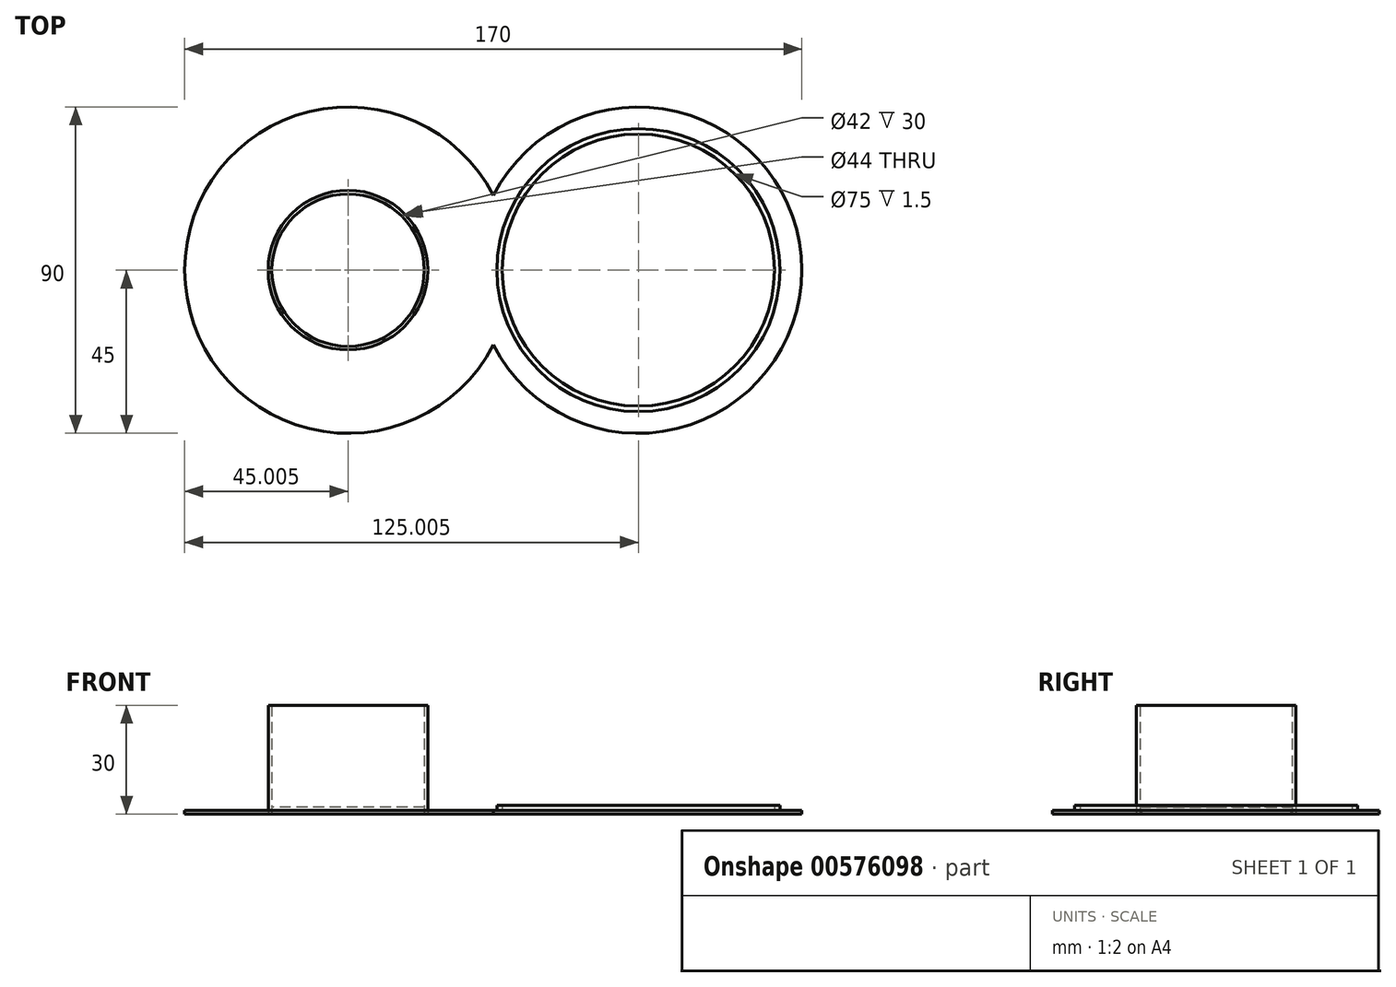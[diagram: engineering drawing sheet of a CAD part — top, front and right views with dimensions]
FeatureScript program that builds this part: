
annotation { "Feature Type Name" : "Feature", "Feature Type Description" : "" }
export const myFeature = defineFeature(function(context is Context, id is Id, definition is map)
    precondition{}
    {
        {
            var Q0;
            Q0=qCreatedBy(makeId("Top.planeOp"),FACE);
            var sketch = newSketch(context, id + "F0", { "sketchPlane" : qUnion([Q0])});
            skCircle(sketch, "E0", {"center": v(-68.95, 0) * mm, "radius": 45 * mm});
            skCircle(sketch, "E1", {"center": v(11.05, 0) * mm, "radius": 45 * mm});
            skCircle(sketch, "E2", {"center": v(-68.95, 0) * mm, "radius": 22 * mm});
            skCircle(sketch, "E3", {"center": v(11.05, 0) * mm, "radius": 39 * mm});
            skCircle(sketch, "E4", {"center": v(-68.95, 0) * mm, "radius": 21 * mm});
            skCircle(sketch, "E5", {"center": v(11.05, 0) * mm, "radius": 37.5 * mm});
            skSolve(sketch);
        }
        {
            var Q0;
            {var subQ3=sQuery(id+"F0.wireOp",EDGE,"E0");var subQ5=sQuery(id+"F0.wireOp",EDGE,"E3");var subQ6=makeQuery(id+"F0.imprint","INTERSECT",VERTEX,{"disambiguationData":[OD(0.0)],"derivedFrom":[subQ3,subQ5]});Q0=makeQuery(id+"F0.imprint","IMPRINT",FACE,{"disambiguationData":[TD([[makeQuery(id+"F0.imprint","IMPRINT",EDGE,{"disambiguationData":[TD([[subQ6,-1.0]])],"derivedFrom":subQ3}),-1.0]])]});}
            var Q1;
            {var subQ0=sQuery(id+"F0.wireOp",EDGE,"E5");var subQ1=sQuery(id+"F0.wireOp",EDGE,"E0");var subQ2=makeQuery(id+"F0.imprint","INTERSECT",VERTEX,{"disambiguationData":[OD(0.0)],"derivedFrom":[subQ1,subQ0]});Q1=makeQuery(id+"F0.imprint","IMPRINT",FACE,{"disambiguationData":[TD([[makeQuery(id+"F0.imprint","IMPRINT",EDGE,{"disambiguationData":[TD([[subQ2,1.0]])],"derivedFrom":subQ1}),-1.0]])]});}
            var Q2;
            Q2=makeQuery(id+"F0.imprint","IMPRINT",FACE,{"disambiguationData":[TD([[makeQuery(id+"F0.imprint","IMPRINT",EDGE,{"derivedFrom":sQuery(id+"F0.wireOp",EDGE,"E2")}),-1.0]])]});
            var Q3;
            {var subQ0=sQuery(id+"F0.wireOp",EDGE,"E3");var subQ1=sQuery(id+"F0.wireOp",EDGE,"E0");var subQ2=makeQuery(id+"F0.imprint","INTERSECT",VERTEX,{"disambiguationData":[OD(0.0)],"derivedFrom":[subQ1,subQ0]});Q3=makeQuery(id+"F0.imprint","IMPRINT",FACE,{"disambiguationData":[TD([[makeQuery(id+"F0.imprint","IMPRINT",EDGE,{"disambiguationData":[TD([[subQ2,-1.0]])],"derivedFrom":subQ1}),1.0]])]});}
            var Q4;
            Q4=makeQuery(id+"F0.imprint","IMPRINT",FACE,{"disambiguationData":[TD([[makeQuery(id+"F0.imprint","IMPRINT",EDGE,{"derivedFrom":sQuery(id+"F0.wireOp",EDGE,"E4")}),1.0]])]});
            var Q5;
            {var subQ0=sQuery(id+"F0.wireOp",EDGE,"E3");var subQ1=sQuery(id+"F0.wireOp",EDGE,"E0");var subQ2=makeQuery(id+"F0.imprint","INTERSECT",VERTEX,{"disambiguationData":[OD(0.0)],"derivedFrom":[subQ1,subQ0]});Q5=makeQuery(id+"F0.imprint","IMPRINT",FACE,{"disambiguationData":[TD([[makeQuery(id+"F0.imprint","IMPRINT",EDGE,{"disambiguationData":[TD([[subQ2,1.0]])],"derivedFrom":subQ1}),-1.0]])]});}
            extrude(context, id + "F1", {"entities" : qUnion([Q0, Q1, Q2, Q3, Q4, Q5]), "depth" : 1 * mm, "offsetDistance" : 25 * mm});
        }
        {
            var Q0;
            Q0=makeQuery(id+"F1.opExtrude","CAP_FACE",FACE,{"disambiguationData":[OSD([sQuery(id+"F0.wireOp",EDGE,"E4")])],"isStart":false});
            extrude(context, id + "F2", {"entities" : qUnion([Q0]), "operationType" : NewBodyOperationType.ADD, "depth" : 1 * mm, "offsetDistance" : 25 * mm});
        }
        {
            var Q0;
            Q0=makeQuery(id+"F0.imprint","IMPRINT",FACE,{"disambiguationData":[TD([[makeQuery(id+"F0.imprint","IMPRINT",EDGE,{"derivedFrom":sQuery(id+"F0.wireOp",EDGE,"E2")}),1.0]])]});
            extrude(context, id + "F3", {"entities" : qUnion([Q0]), "depth" : 30 * mm, "offsetDistance" : 25 * mm});
        }
        {
            var Q0;
            {var subQ0=sQuery(id+"F0.wireOp",EDGE,"E5");var subQ1=sQuery(id+"F0.wireOp",EDGE,"E0");var subQ2=makeQuery(id+"F0.imprint","INTERSECT",VERTEX,{"disambiguationData":[OD(0.0)],"derivedFrom":[subQ1,subQ0]});Q0=makeQuery(id+"F0.imprint","IMPRINT",FACE,{"disambiguationData":[TD([[makeQuery(id+"F0.imprint","IMPRINT",EDGE,{"disambiguationData":[TD([[subQ2,1.0]])],"derivedFrom":subQ1}),1.0]])]});}
            extrude(context, id + "F4", {"entities" : qUnion([Q0]), "operationType" : NewBodyOperationType.ADD, "depth" : 1 * mm, "offsetDistance" : 25 * mm});
        }
        {
            var Q0;
            {var subQ0=sQuery(id+"F0.wireOp",EDGE,"E3");var subQ1=sQuery(id+"F0.wireOp",EDGE,"E0");var subQ2=makeQuery(id+"F0.imprint","INTERSECT",VERTEX,{"disambiguationData":[OD(0.0)],"derivedFrom":[subQ1,subQ0]});Q0=makeQuery(id+"F0.imprint","IMPRINT",FACE,{"disambiguationData":[TD([[makeQuery(id+"F0.imprint","IMPRINT",EDGE,{"disambiguationData":[TD([[subQ2,1.0]])],"derivedFrom":subQ1}),-1.0]])]});}
            var Q1;
            {var subQ0=sQuery(id+"F0.wireOp",EDGE,"E3");var subQ1=sQuery(id+"F0.wireOp",EDGE,"E0");var subQ2=makeQuery(id+"F0.imprint","INTERSECT",VERTEX,{"disambiguationData":[OD(0.0)],"derivedFrom":[subQ1,subQ0]});Q1=makeQuery(id+"F0.imprint","IMPRINT",FACE,{"disambiguationData":[TD([[makeQuery(id+"F0.imprint","IMPRINT",EDGE,{"disambiguationData":[TD([[subQ2,1.0]])],"derivedFrom":subQ1}),1.0]])]});}
            extrude(context, id + "F5", {"entities" : qUnion([Q0, Q1]), "operationType" : NewBodyOperationType.ADD, "depth" : 2.5 * mm, "offsetDistance" : 25 * mm});
        }
    });
